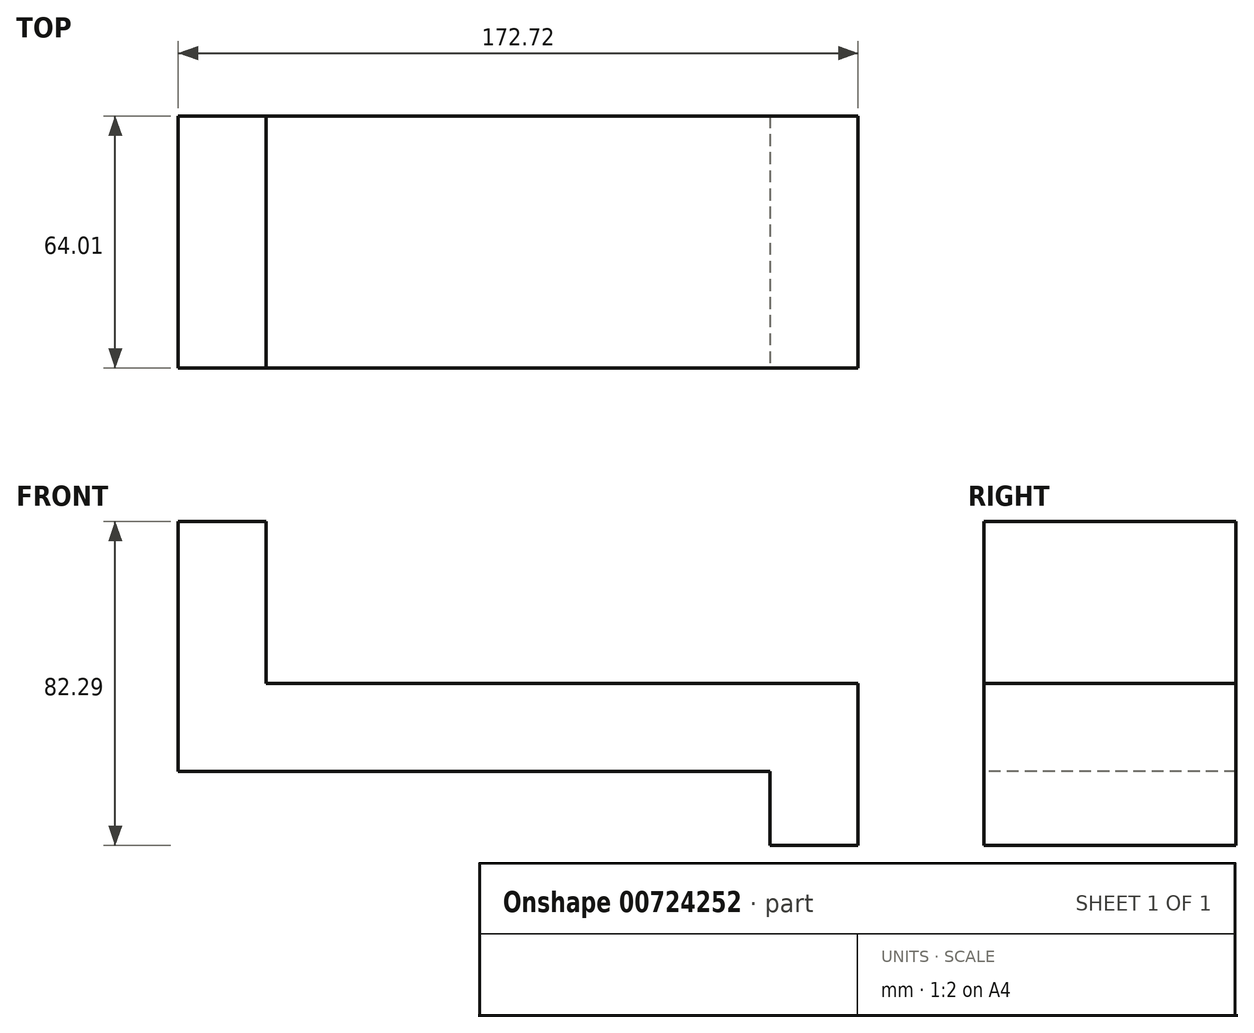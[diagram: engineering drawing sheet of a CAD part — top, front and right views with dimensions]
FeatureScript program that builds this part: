
annotation { "Feature Type Name" : "Feature", "Feature Type Description" : "" }
export const myFeature = defineFeature(function(context is Context, id is Id, definition is map)
    precondition{}
    {
        {
            var Q0;
            Q0=qCreatedBy(makeId("Front.planeOp"),FACE);
            var sketch = newSketch(context, id + "F0", { "sketchPlane" : qUnion([Q0])});
            skLineSegment(sketch, "E0", {"start": v(-55.24, 66.17) * mm, "end": v(-55.24, 2.67) * mm});
            skLineSegment(sketch, "E1", {"start": v(-55.24, 66.17) * mm, "end": v(-32.89, 66.17) * mm});
            skLineSegment(sketch, "E2", {"start": v(-55.24, 2.67) * mm, "end": v(95.13, 2.67) * mm});
            skLineSegment(sketch, "E3", {"start": v(-32.89, 66.17) * mm, "end": v(-32.89, 25.03) * mm});
            skLineSegment(sketch, "E4", {"start": v(95.13, 2.67) * mm, "end": v(95.13, -16.12) * mm});
            skLineSegment(sketch, "E5", {"start": v(95.13, -16.12) * mm, "end": v(117.48, -16.12) * mm});
            skLineSegment(sketch, "E6", {"start": v(117.48, -16.12) * mm, "end": v(117.48, 25.03) * mm});
            skLineSegment(sketch, "E7", {"start": v(117.48, 25.03) * mm, "end": v(-32.89, 25.03) * mm});
            skSolve(sketch);
        }
        {
            var Q0;
            Q0=makeQuery(id+"F0.imprint","IMPRINT",FACE,{"disambiguationData":[TD([[makeQuery(id+"F0.imprint","IMPRINT",EDGE,{"derivedFrom":sQuery(id+"F0.wireOp",EDGE,"E0")}),1.0]])]});
            extrude(context, id + "F1", {"entities" : qUnion([Q0]), "oppositeDirection" : true, "depth" : 64 * mm, "offsetDistance" : 25.4 * mm});
        }
    });
